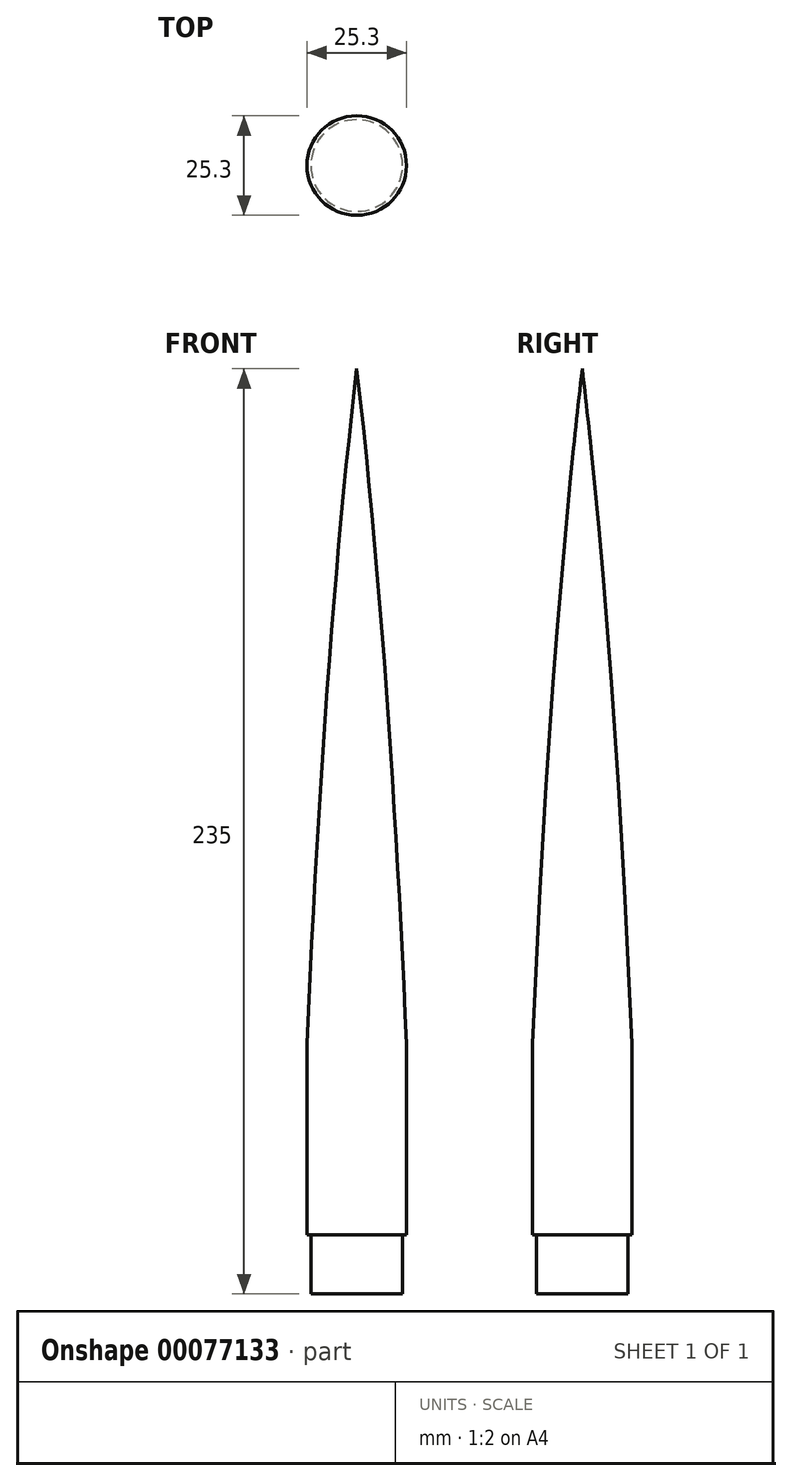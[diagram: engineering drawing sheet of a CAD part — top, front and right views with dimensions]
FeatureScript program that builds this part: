
annotation { "Feature Type Name" : "Feature", "Feature Type Description" : "" }
export const myFeature = defineFeature(function(context is Context, id is Id, definition is map)
    precondition{}
    {
        {
            var Q0;
            Q0=qCreatedBy(makeId("Front.planeOp"),FACE);
            var sketch = newSketch(context, id + "F0", { "sketchPlane" : qUnion([Q0])});
            skLineSegment(sketch, "E0.bottom", {"start": v(-11.65, 0) * mm, "end": v(-12.65, 0) * mm});
            skLineSegment(sketch, "E0.left", {"start": v(0, 0) * mm, "end": v(0, 220) * mm});
            skLineSegment(sketch, "E0.right", {"start": v(-12.65, 0) * mm, "end": v(-12.65, 48.27) * mm});
            skLineSegment(sketch, "E1", {"start": v(0, 0) * mm, "end": v(0, 478.85) * mm, "construction": true});
            skEllipticalArc(sketch, "E2", {});
            skPoint(sketch, "E3.orphan", {"position": v(-12.65, 220) * mm});
            skLineSegment(sketch, "E4.top", {"start": v(-11.65, -15) * mm, "end": v(0, -15) * mm});
            skLineSegment(sketch, "E4.left", {"start": v(-11.65, 0) * mm, "end": v(-11.65, -15) * mm});
            skLineSegment(sketch, "E4.right", {"start": v(0, 0) * mm, "end": v(0, -15) * mm});
            const initialGuessF0  = {"E2": [0.008984643965959549, 0, 0.030282434630274097, 0.9995413819111559, 0.29539129621346616, 0.02339185779753911, 0.7324891129531036, 1.4089898555643126]};
            skSetInitialGuess(sketch, initialGuessF0);
            skSolve(sketch);
        }
        {
            var Q0;
            Q0=makeQuery(id+"F0.imprint","IMPRINT",FACE,{"disambiguationData":[TD([[makeQuery(id+"F0.imprint","IMPRINT",EDGE,{"derivedFrom":sQuery(id+"F0.wireOp",EDGE,"E0.bottom")}),-1.0]])]});
            var Q1;
            Q1=sQuery(id+"F0.wireOp",EDGE,"E0.left");
            revolve(context, id + "F1", {"entities" : qUnion([Q0]), "axis" : qUnion([Q1]), "revolveType" : RevolveType.FULL});
        }
        {
            var Q0;
            Q0=makeQuery(id+"F1.opRevolve","SWEPT_EDGE",EDGE,{"disambiguationData":[OSD([sQuery(id+"F0.wireOp",EDGE,"E0.right"),sQuery(id+"F0.wireOp",EDGE,"E2")])]});
            fillet(context, id + "F2", {"entities" : qUnion([Q0]), "radius" : 10 * mm, "tangentPropagation" : true, "allowEdgeOverflow" : false});
        }
    });
